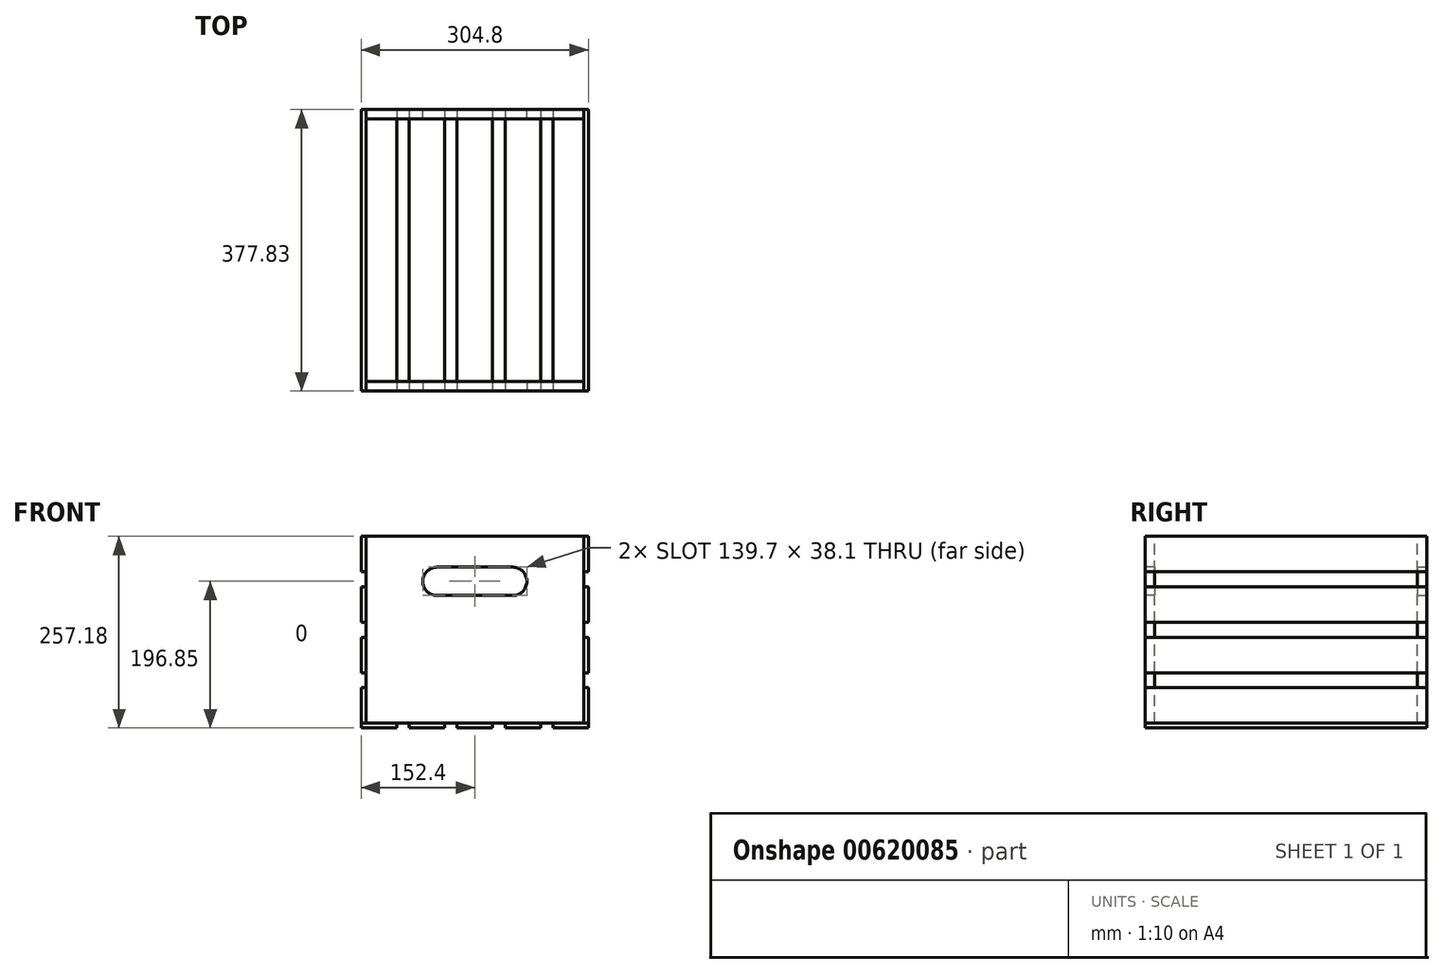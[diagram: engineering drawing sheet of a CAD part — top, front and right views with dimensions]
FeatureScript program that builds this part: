
annotation { "Feature Type Name" : "Feature", "Feature Type Description" : "" }
export const myFeature = defineFeature(function(context is Context, id is Id, definition is map)
    precondition{}
    {
        {
            var Q0;
            Q0=qCreatedBy(makeId("Front.planeOp"),FACE);
            var sketch = newSketch(context, id + "F0", { "sketchPlane" : qUnion([Q0])});
            skLineSegment(sketch, "E0", {"start": v(-146.05, 0) * mm, "end": v(146.05, 0) * mm});
            skLineSegment(sketch, "E1", {"start": v(146.05, 0) * mm, "end": v(146.05, 250.83) * mm});
            skLineSegment(sketch, "E2", {"start": v(146.05, 250.82) * mm, "end": v(-146.05, 250.82) * mm});
            skLineSegment(sketch, "E3", {"start": v(-146.05, 250.83) * mm, "end": v(-146.05, 0) * mm});
            skArc(sketch, "E4", {"start": v(-50.8, 209.55) * mm, "mid": v(-69.85, 190.5) * mm, "end": v(-50.8, 171.45) * mm});
            skLineSegment(sketch, "E5", {"start": v(0, 0) * mm, "end": v(0, 250.82) * mm, "construction": true});
            skArc(sketch, "E6.MirrorC", {"start": v(50.8, 209.55) * mm, "mid": v(69.85, 190.5) * mm, "end": v(50.8, 171.45) * mm});
            skLineSegment(sketch, "E7", {"start": v(-50.8, 209.55) * mm, "end": v(50.8, 209.55) * mm});
            skLineSegment(sketch, "E8", {"start": v(50.8, 171.45) * mm, "end": v(-50.8, 171.45) * mm});
            skSolve(sketch);
        }
        {
            var Q0;
            Q0 = qSketchRegion(id + "F0", true);
            extrude(context, id + "F1", {"entities" : qUnion([Q0]), "oppositeDirection" : true, "depth" : 12.7 * mm, "offsetDistance" : 25.4 * mm});
        }
        {
            var Q0;
            Q0=makeQuery(id+"F1.opExtrude","CAP_FACE",FACE,{"disambiguationData":[OSD([sQuery(id+"F0.wireOp",EDGE,"E0"),sQuery(id+"F0.wireOp",EDGE,"E1"),sQuery(id+"F0.wireOp",EDGE,"E2"),sQuery(id+"F0.wireOp",EDGE,"E3"),sQuery(id+"F0.wireOp",EDGE,"E4"),sQuery(id+"F0.wireOp",EDGE,"E6.MirrorC"),sQuery(id+"F0.wireOp",EDGE,"E7"),sQuery(id+"F0.wireOp",EDGE,"E8")])],"isStart":true});
            cPlane(context, id + "F2", {"entities" : qUnion([Q0]), "cplaneType" : CPlaneType.OFFSET, "offset" : 188.9 * mm, "oppositeDirection" : true, "width" : 152.4 * mm, "height" : 152.4 * mm});
        }
        {
            var Q0;
            Q0=makeQuery(id+"F1.opExtrude","SWEPT_BODY",BODY,{"disambiguationData":[OSD([sQuery(id+"F0.wireOp",EDGE,"E0"),sQuery(id+"F0.wireOp",EDGE,"E1"),sQuery(id+"F0.wireOp",EDGE,"E2"),sQuery(id+"F0.wireOp",EDGE,"E3"),sQuery(id+"F0.wireOp",EDGE,"E4"),sQuery(id+"F0.wireOp",EDGE,"E6.MirrorC"),sQuery(id+"F0.wireOp",EDGE,"E7"),sQuery(id+"F0.wireOp",EDGE,"E8")])]});
            var Q1;
            Q1=qCreatedBy(id+"F2.planeOp",FACE);
            mirror(context, id + "F3", {"entities" : qUnion([Q0]), "mirrorPlane" : qUnion([Q1])});
        }
        {
            var Q0;
            Q0=makeQuery(id+"F1.opExtrude","SWEPT_FACE",FACE,{"disambiguationData":[OSD([sQuery(id+"F0.wireOp",EDGE,"E1")])]});
            var sketch = newSketch(context, id + "F4", { "sketchPlane" : qUnion([Q0])});
            skLineSegment(sketch, "E9.0", {"start": v(0, 0) * mm, "end": v(0, 47.62) * mm});
            skLineSegment(sketch, "E9.1", {"start": v(377.83, 0) * mm, "end": v(377.83, 47.63) * mm});
            skLineSegment(sketch, "E10", {"start": v(0, 250.83) * mm, "end": v(377.83, 250.83) * mm});
            skLineSegment(sketch, "E11", {"start": v(0, 0) * mm, "end": v(377.83, 0) * mm});
            skLineSegment(sketch, "E12", {"start": v(0, 47.62) * mm, "end": v(377.83, 47.63) * mm});
            skLineSegment(sketch, "E13", {"start": v(0, 67.73) * mm, "end": v(377.83, 67.73) * mm});
            skLineSegment(sketch, "E14", {"start": v(0, 115.36) * mm, "end": v(377.83, 115.36) * mm});
            skLineSegment(sketch, "E15", {"start": v(0, 135.47) * mm, "end": v(377.83, 135.47) * mm});
            skLineSegment(sketch, "E16", {"start": v(0, 183.1) * mm, "end": v(377.83, 183.1) * mm});
            skLineSegment(sketch, "E17", {"start": v(0, 203.2) * mm, "end": v(377.83, 203.2) * mm});
            skLineSegment(sketch, "E18.trimOffspring", {"start": v(377.83, 203.2) * mm, "end": v(377.83, 250.83) * mm});
            skLineSegment(sketch, "E19.trimOffspring", {"start": v(377.83, 135.47) * mm, "end": v(377.83, 183.1) * mm});
            skLineSegment(sketch, "E20.trimOffspring", {"start": v(377.83, 67.73) * mm, "end": v(377.83, 115.36) * mm});
            skLineSegment(sketch, "E21.trimOffspring", {"start": v(0, 67.73) * mm, "end": v(0, 115.36) * mm});
            skLineSegment(sketch, "E22.trimOffspring", {"start": v(0, 135.47) * mm, "end": v(0, 183.1) * mm});
            skLineSegment(sketch, "E23.trimOffspring", {"start": v(0, 203.2) * mm, "end": v(0, 250.83) * mm});
            skLineSegment(sketch, "E24", {"start": v(377.83, 203.2) * mm, "end": v(377.83, 183.1) * mm, "construction": true});
            skLineSegment(sketch, "E25", {"start": v(377.83, 135.47) * mm, "end": v(377.83, 115.36) * mm, "construction": true});
            skLineSegment(sketch, "E26", {"start": v(377.83, 67.73) * mm, "end": v(377.83, 47.63) * mm, "construction": true});
            skSolve(sketch);
        }
        {
            var Q0;
            Q0 = qSketchRegion(id + "F4", true);
            extrude(context, id + "F5", {"entities" : qUnion([Q0]), "depth" : 6.35 * mm, "offsetDistance" : 25.4 * mm});
        }
        {
            var Q0;
            Q0=makeQuery(id+"F5.opExtrude","SWEPT_BODY",BODY,{"disambiguationData":[OSD([sQuery(id+"F4.wireOp",EDGE,"E15"),sQuery(id+"F4.wireOp",EDGE,"E16"),sQuery(id+"F4.wireOp",EDGE,"E19.trimOffspring"),sQuery(id+"F4.wireOp",EDGE,"E22.trimOffspring")])]});
            var Q1;
            Q1=makeQuery(id+"F5.opExtrude","SWEPT_BODY",BODY,{"disambiguationData":[OSD([sQuery(id+"F4.wireOp",EDGE,"E10"),sQuery(id+"F4.wireOp",EDGE,"E17"),sQuery(id+"F4.wireOp",EDGE,"E18.trimOffspring"),sQuery(id+"F4.wireOp",EDGE,"E23.trimOffspring")])]});
            var Q2;
            Q2=makeQuery(id+"F5.opExtrude","SWEPT_BODY",BODY,{"disambiguationData":[OSD([sQuery(id+"F4.wireOp",EDGE,"E13"),sQuery(id+"F4.wireOp",EDGE,"E14"),sQuery(id+"F4.wireOp",EDGE,"E20.trimOffspring"),sQuery(id+"F4.wireOp",EDGE,"E21.trimOffspring")])]});
            var Q3;
            Q3=makeQuery(id+"F5.opExtrude","SWEPT_BODY",BODY,{"disambiguationData":[OSD([sQuery(id+"F4.wireOp",EDGE,"E9.0"),sQuery(id+"F4.wireOp",EDGE,"E9.1"),sQuery(id+"F4.wireOp",EDGE,"E11"),sQuery(id+"F4.wireOp",EDGE,"E12")])]});
            var Q4;
            Q4=qCreatedBy(makeId("Right.planeOp"),FACE);
            mirror(context, id + "F6", {"entities" : qUnion([Q0, Q1, Q2, Q3]), "mirrorPlane" : qUnion([Q4])});
        }
        {
            var Q0;
            Q0=makeQuery(id+"F1.opExtrude","CAP_FACE",FACE,{"disambiguationData":[OSD([sQuery(id+"F0.wireOp",EDGE,"E0"),sQuery(id+"F0.wireOp",EDGE,"E1"),sQuery(id+"F0.wireOp",EDGE,"E2"),sQuery(id+"F0.wireOp",EDGE,"E3"),sQuery(id+"F0.wireOp",EDGE,"E4"),sQuery(id+"F0.wireOp",EDGE,"E6.MirrorC"),sQuery(id+"F0.wireOp",EDGE,"E7"),sQuery(id+"F0.wireOp",EDGE,"E8")])],"isStart":true});
            var sketch = newSketch(context, id + "F7", { "sketchPlane" : qUnion([Q0])});
            skLineSegment(sketch, "E27.0", {"start": v(-146.05, 0) * mm, "end": v(-104.77, 0) * mm});
            skLineSegment(sketch, "E28.0", {"start": v(152.4, 0) * mm, "end": v(146.05, 0) * mm});
            skLineSegment(sketch, "E29.0", {"start": v(-152.4, 0) * mm, "end": v(-146.05, 0) * mm});
            skLineSegment(sketch, "E30", {"start": v(-152.4, 0) * mm, "end": v(-152.4, -6.35) * mm});
            skLineSegment(sketch, "E31", {"start": v(-152.4, -6.35) * mm, "end": v(-104.77, -6.35) * mm});
            skLineSegment(sketch, "E32", {"start": v(152.4, -6.35) * mm, "end": v(152.4, 0) * mm});
            skLineSegment(sketch, "E33", {"start": v(104.77, 0) * mm, "end": v(104.77, -6.35) * mm});
            skLineSegment(sketch, "E34", {"start": v(88.1, 0) * mm, "end": v(88.1, -6.35) * mm});
            skLineSegment(sketch, "E35", {"start": v(40.48, 0) * mm, "end": v(40.48, -6.35) * mm});
            skLineSegment(sketch, "E36", {"start": v(23.81, 0) * mm, "end": v(23.81, -6.35) * mm});
            skLineSegment(sketch, "E37", {"start": v(-23.81, 0) * mm, "end": v(-23.81, -6.35) * mm});
            skLineSegment(sketch, "E38", {"start": v(-40.48, 0) * mm, "end": v(-40.48, -6.35) * mm});
            skLineSegment(sketch, "E39", {"start": v(-88.1, 0) * mm, "end": v(-88.1, -6.35) * mm});
            skLineSegment(sketch, "E40", {"start": v(-104.77, 0) * mm, "end": v(-104.77, -6.35) * mm});
            skLineSegment(sketch, "E41.trimOffspring", {"start": v(104.77, 0) * mm, "end": v(146.05, 0) * mm});
            skLineSegment(sketch, "E42.trimOffspring", {"start": v(104.77, -6.35) * mm, "end": v(152.4, -6.35) * mm});
            skLineSegment(sketch, "E43.trimOffspring", {"start": v(40.48, 0) * mm, "end": v(88.1, 0) * mm});
            skLineSegment(sketch, "E44.trimOffspring", {"start": v(40.48, -6.35) * mm, "end": v(88.1, -6.35) * mm});
            skLineSegment(sketch, "E45.trimOffspring", {"start": v(-23.81, 0) * mm, "end": v(23.81, 0) * mm});
            skLineSegment(sketch, "E46.trimOffspring", {"start": v(-23.81, -6.35) * mm, "end": v(23.81, -6.35) * mm});
            skLineSegment(sketch, "E47.trimOffspring", {"start": v(-88.1, 0) * mm, "end": v(-40.48, 0) * mm});
            skLineSegment(sketch, "E48.trimOffspring", {"start": v(-88.1, -6.35) * mm, "end": v(-40.48, -6.35) * mm});
            skLineSegment(sketch, "E49", {"start": v(-104.77, -6.35) * mm, "end": v(-88.1, -6.35) * mm, "construction": true});
            skLineSegment(sketch, "E50", {"start": v(-40.48, -6.35) * mm, "end": v(-23.81, -6.35) * mm, "construction": true});
            skLineSegment(sketch, "E51", {"start": v(23.81, -6.35) * mm, "end": v(40.48, -6.35) * mm, "construction": true});
            skLineSegment(sketch, "E52", {"start": v(88.1, -6.35) * mm, "end": v(104.77, -6.35) * mm, "construction": true});
            skSolve(sketch);
        }
        {
            var Q0;
            Q0 = qSketchRegion(id + "F7", true);
            var Q1;
            Q1=makeQuery(id+"F3.opPattern","COPY",FACE,{"derivedFrom":makeQuery(id+"F1.opExtrude","CAP_FACE",FACE,{"disambiguationData":[OSD([sQuery(id+"F0.wireOp",EDGE,"E0"),sQuery(id+"F0.wireOp",EDGE,"E1"),sQuery(id+"F0.wireOp",EDGE,"E2"),sQuery(id+"F0.wireOp",EDGE,"E3"),sQuery(id+"F0.wireOp",EDGE,"E4"),sQuery(id+"F0.wireOp",EDGE,"E6.MirrorC"),sQuery(id+"F0.wireOp",EDGE,"E7"),sQuery(id+"F0.wireOp",EDGE,"E8")])],"isStart":true}),"instanceName":"1"});
            extrude(context, id + "F8", {"entities" : qUnion([Q0]), "endBound" : BoundingType.UP_TO_SURFACE, "oppositeDirection" : true, "depth" : 25.4 * mm, "endBoundEntityFace" : qUnion([Q1]), "offsetDistance" : 25.4 * mm});
        }
    });
